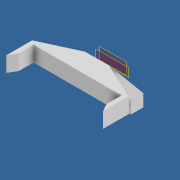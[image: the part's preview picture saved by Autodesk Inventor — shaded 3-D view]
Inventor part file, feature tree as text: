
AUTODESK INVENTOR PART (.ipt)
format: ipt  version: 2020 (Build 240168000, 168)  size: 200,192 bytes
history: native  units: mm
features: extrude x4, sketch x4, chamfer x3, plane x2, other x2, mirror x1, fillet x1, loft x1
ambient origin geometry x8: Origin, YZ Plane, XZ Plane, XY Plane, X Axis, Y Axis, Z Axis, Center Point
bodies: Solid1 (feature_tree)
feature tree (18):
  extrude  "Extrusion1"  Depth=10.0mm
  chamfer  "Chamfer1"  Distance=13.0mm
  chamfer  "Chamfer2"  Distance=24.0mm Angle=45.0deg
  extrude  "Extrusion2"  Depth=3.0mm
  chamfer  "Chamfer4"  Distance=15.0mm
  plane  "Work Plane1"
  mirror  "Mirror3"
  plane  "Work Plane8"
  extrude  "Extrusion9"  Depth=10.0mm
  extrude  "Extrusion10"  Depth=10.5mm
  fillet  "Fillet2"  Radius=24.0mm
  loft  "Loft7"
  sketch  "Sketch1"  dims[d1=64.0mm d2=10.0mm d3=13.0mm d4=0.0mm d5=24.0mm d6=11.0mm d7=45.0deg]
  sketch  "Sketch2"  dims[d8=24.0mm d9=11.0mm d10=45.0deg d14=3.0mm]
  sketch  "Sketch19"  dims[d15=10.0mm d16=15.0mm d17=0.0mm]
  sketch  "Sketch20"  dims[d18=3.0mm d19=10.0mm d20=60.0deg d21=10.0mm d94=10.5mm d95=24.0mm d96=8.0mm d97=13.0mm d98=8.0mm d99=0.0mm d100=5.0mm d101=5.0mm d102=5.0mm d103=8.0mm d104=8.0mm d105=4.0mm d106=8.0mm d107=0.0mm d108=0.7mm d109=0.0mm d110=90.0deg d111=0.0mm d112=90.0deg]
  other  "Edges5"
  other  "Edges6"
